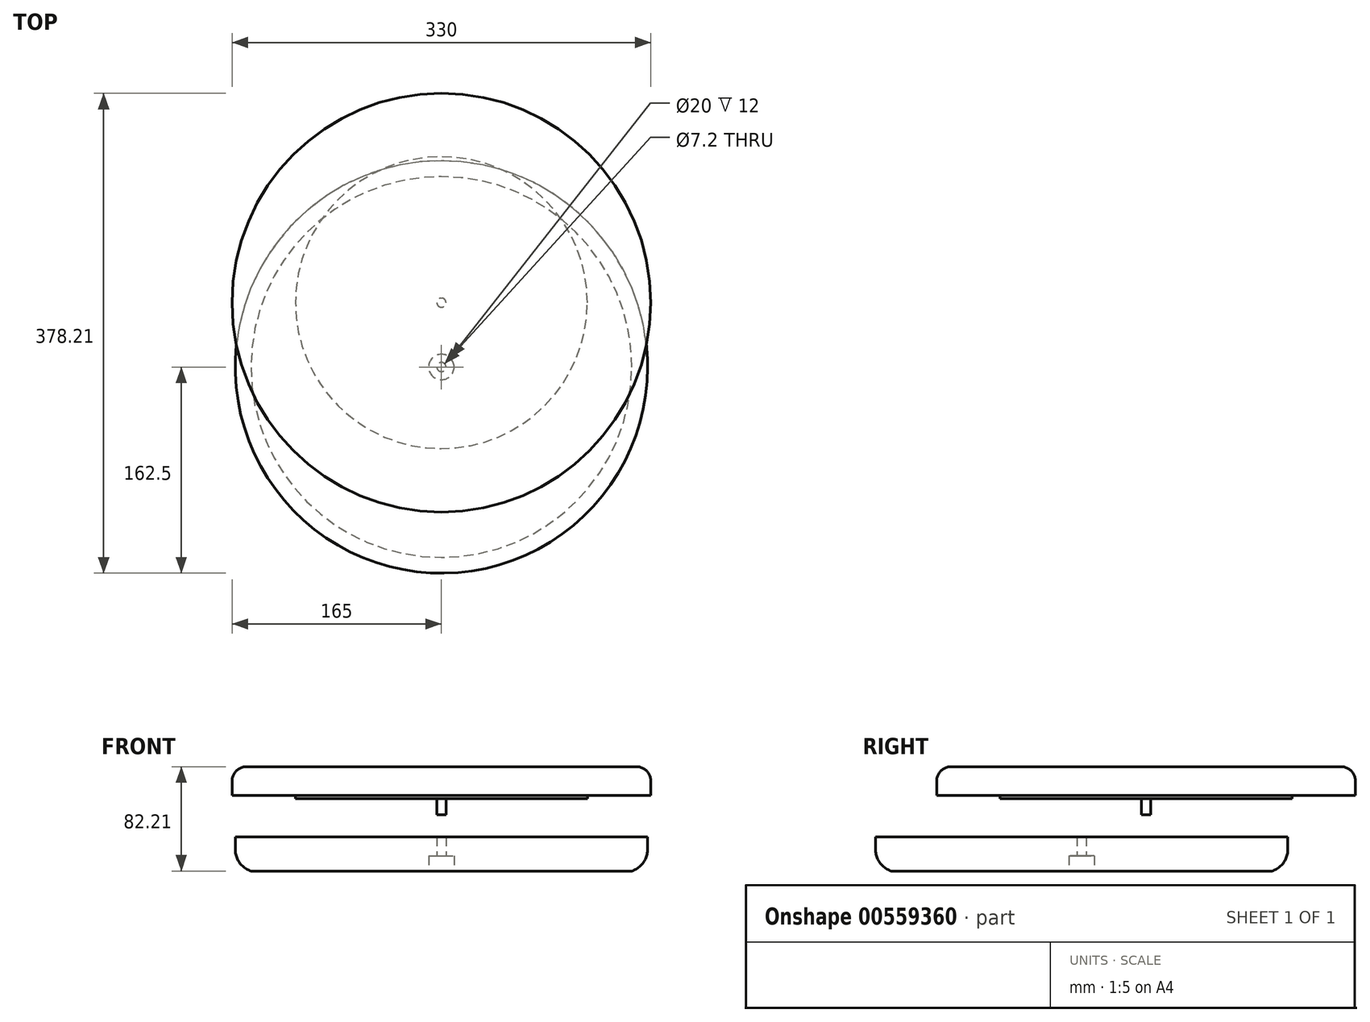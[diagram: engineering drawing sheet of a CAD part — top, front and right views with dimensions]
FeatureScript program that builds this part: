
annotation { "Feature Type Name" : "Feature", "Feature Type Description" : "" }
export const myFeature = defineFeature(function(context is Context, id is Id, definition is map)
    precondition{}
    {
        {
            var Q0;
            Q0=qCreatedBy(makeId("Top.planeOp"),FACE);
            var sketch = newSketch(context, id + "F0", { "sketchPlane" : qUnion([Q0])});
            skCircle(sketch, "E0", {"center": v(0, 50.71) * mm, "radius": 165 * mm});
            skSolve(sketch);
        }
        {
            var Q0;
            Q0=makeQuery(id+"F0.imprint","IMPRINT",FACE,{"disambiguationData":[TD([[makeQuery(id+"F0.imprint","IMPRINT",EDGE,{"derivedFrom":sQuery(id+"F0.wireOp",EDGE,"E0")}),1.0]])]});
            extrude(context, id + "F1", {"entities" : qUnion([Q0]), "depth" : 22.5 * mm, "offsetDistance" : 25.4 * mm});
        }
        {
            var Q0;
            Q0=makeQuery(id+"F1.opExtrude","CAP_EDGE",EDGE,{"disambiguationData":[OSD([sQuery(id+"F0.wireOp",EDGE,"E0")])],"isStart":false});
            fillet(context, id + "F2", {"entities" : qUnion([Q0]), "radius" : 11.25 * mm, "tangentPropagation" : true, "allowEdgeOverflow" : false});
        }
        {
            var Q0;
            Q0=makeQuery(id+"F1.opExtrude","CAP_FACE",FACE,{"disambiguationData":[OSD([sQuery(id+"F0.wireOp",EDGE,"E0")])],"isStart":true});
            var sketch = newSketch(context, id + "F3", { "sketchPlane" : qUnion([Q0])});
            skCircle(sketch, "E1", {"center": v(0, -50.71) * mm, "radius": 165 * mm});
            skPoint(sketch, "E1.first.point", {"position": v(28.12, 111.87) * mm});
            skPoint(sketch, "E1.second.point", {"position": v(60.24, -204.32) * mm});
            skPoint(sketch, "E1.third.point", {"position": v(-161.52, -84.41) * mm});
            skCircle(sketch, "E2", {"center": v(0, -50.71) * mm, "radius": 115 * mm});
            skSolve(sketch);
        }
        {
            var Q0;
            Q0=makeQuery(id+"F3.imprint","IMPRINT",FACE,{"disambiguationData":[TD([[makeQuery(id+"F3.imprint","IMPRINT",EDGE,{"derivedFrom":sQuery(id+"F3.wireOp",EDGE,"E2")}),1.0]])]});
            extrude(context, id + "F4", {"entities" : qUnion([Q0]), "operationType" : NewBodyOperationType.ADD, "depth" : 2.81 * mm, "offsetDistance" : 25.4 * mm});
        }
        {
            var Q0;
            Q0=qCreatedBy(makeId("Front.planeOp"),FACE);
            var sketch = newSketch(context, id + "F5", { "sketchPlane" : qUnion([Q0])});
            skLineSegment(sketch, "E3", {"start": v(0, -32.7) * mm, "end": v(162.5, -32.7) * mm});
            skLineSegment(sketch, "E4", {"start": v(0, -32.7) * mm, "end": v(0, -59.7) * mm});
            skLineSegment(sketch, "E5", {"start": v(162.5, -32.7) * mm, "end": v(162.5, -42.7) * mm});
            skLineSegment(sketch, "E6", {"start": v(0, -59.7) * mm, "end": v(150, -59.7) * mm});
            skArc(sketch, "E7", {"start": v(150, -59.7) * mm, "mid": v(159.04, -53.26) * mm, "end": v(162.5, -42.7) * mm});
            skSolve(sketch);
        }
        {
            var Q0;
            Q0=makeQuery(id+"F5.imprint","IMPRINT",FACE,{"disambiguationData":[TD([[makeQuery(id+"F5.imprint","IMPRINT",EDGE,{"derivedFrom":sQuery(id+"F5.wireOp",EDGE,"E3")}),-1.0]])]});
            var Q1;
            Q1=sQuery(id+"F5.wireOp",EDGE,"E4");
            revolve(context, id + "F6", {"entities" : qUnion([Q0]), "axis" : qUnion([Q1]), "revolveType" : RevolveType.FULL});
        }
        {
            var Q0;
            Q0=makeQuery(id+"F6.opRevolve","SWEPT_FACE",FACE,{"disambiguationData":[OSD([sQuery(id+"F5.wireOp",EDGE,"E6")])]});
            var sketch = newSketch(context, id + "F7", { "sketchPlane" : qUnion([Q0])});
            skCircle(sketch, "E8", {"center": v(0, 0) * mm, "radius": 150 * mm});
            skPoint(sketch, "E8.first.point", {"position": v(-38.11, -145.08) * mm});
            skPoint(sketch, "E8.second.point", {"position": v(-35.1, 145.84) * mm});
            skPoint(sketch, "E8.third.point", {"position": v(148.6, 20.4) * mm});
            skCircle(sketch, "E9", {"center": v(0, 0) * mm, "radius": 10 * mm});
            skSolve(sketch);
        }
        {
            var Q0;
            Q0=makeQuery(id+"F7.imprint","IMPRINT",FACE,{"disambiguationData":[TD([[makeQuery(id+"F7.imprint","IMPRINT",EDGE,{"derivedFrom":sQuery(id+"F7.wireOp",EDGE,"E9")}),1.0]])]});
            extrude(context, id + "F8", {"entities" : qUnion([Q0]), "operationType" : NewBodyOperationType.REMOVE, "oppositeDirection" : true, "depth" : 12 * mm, "offsetDistance" : 25.4 * mm});
        }
        {
            var Q0;
            Q0=makeQuery(id+"F8.boolean.opBoolean","COPY",FACE,{"derivedFrom":makeQuery(id+"F8.opExtrude","CAP_FACE",FACE,{"disambiguationData":[OSD([sQuery(id+"F7.wireOp",EDGE,"E9")])],"isStart":false})});
            var sketch = newSketch(context, id + "F9", { "sketchPlane" : qUnion([Q0])});
            skCircle(sketch, "E10", {"center": v(0, 0) * mm, "radius": 10 * mm});
            skPoint(sketch, "E10.first.point", {"position": v(-1.32, -9.91) * mm});
            skPoint(sketch, "E10.second.point", {"position": v(-0.95, 9.95) * mm});
            skPoint(sketch, "E10.third.point", {"position": v(-9.99, -0.45) * mm});
            skCircle(sketch, "E11", {"center": v(0, 0) * mm, "radius": 3.6 * mm});
            skSolve(sketch);
        }
        {
            var Q0;
            Q0=makeQuery(id+"F9.imprint","IMPRINT",FACE,{"disambiguationData":[TD([[makeQuery(id+"F9.imprint","IMPRINT",EDGE,{"derivedFrom":sQuery(id+"F9.wireOp",EDGE,"E11")}),1.0]])]});
            extrude(context, id + "F10", {"entities" : qUnion([Q0]), "operationType" : NewBodyOperationType.REMOVE, "oppositeDirection" : true, "depth" : 25.4 * mm, "offsetDistance" : 25.4 * mm});
        }
        {
            var Q0;
            Q0=makeQuery(id+"F4.opExtrude","CAP_FACE",FACE,{"disambiguationData":[OSD([sQuery(id+"F3.wireOp",EDGE,"E2")])],"isStart":false});
            var sketch = newSketch(context, id + "F11", { "sketchPlane" : qUnion([Q0])});
            skCircle(sketch, "E12", {"center": v(0, -50.71) * mm, "radius": 115 * mm});
            skPoint(sketch, "E12.first.point", {"position": v(90.57, -121.58) * mm});
            skPoint(sketch, "E12.second.point", {"position": v(-27.41, 60.97) * mm});
            skPoint(sketch, "E12.third.point", {"position": v(61.86, 46.23) * mm});
            skCircle(sketch, "E13", {"center": v(0, -50.71) * mm, "radius": 3.6 * mm});
            skSolve(sketch);
        }
        {
            var Q0;
            Q0=makeQuery(id+"F11.imprint","IMPRINT",FACE,{"disambiguationData":[TD([[makeQuery(id+"F11.imprint","IMPRINT",EDGE,{"derivedFrom":sQuery(id+"F11.wireOp",EDGE,"E13")}),1.0]])]});
            extrude(context, id + "F12", {"entities" : qUnion([Q0]), "operationType" : NewBodyOperationType.ADD, "depth" : 12.47 * mm, "offsetDistance" : 25.4 * mm});
        }
    });
